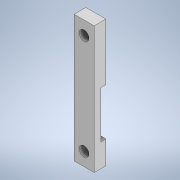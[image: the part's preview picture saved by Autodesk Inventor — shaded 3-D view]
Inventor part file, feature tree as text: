
AUTODESK INVENTOR PART (.ipt)
format: ipt  version: 2021 (Build 250183000, 183)  size: 128,000 bytes
history: native  units: in
note: dims shown in document units (in); Inventor stores cm internally (conversion verified against a paired STEP export)
features: other x3, extrude x2, sketch x2, reference x2, projected_geometry x2, plane x1
ambient origin geometry x8: Origin, YZ Plane, XZ Plane, XY Plane, X Axis, Y Axis, Z Axis, Center Point
bodies: Solid1 (feature_tree)
feature tree (12):
  plane  "Work Plane1"
  extrude  "Extrusion1"  Depth=0.0787in
  extrude  "Extrusion2"  Depth=0.0787in
  sketch  "Sketch1"  dims[d0=0.1575in d1=0.0787in]
  reference  "Reference1"
  reference  "Reference2"
  sketch  "Sketch2"  dims[d2=0.0394in d3=0.1575in d4=0.1181in d6=0.1181in d7=0.0591in d8=0.0in d9=0.0787in d10=0.0in]
  projected_geometry  "Projected Loop1"
  projected_geometry  "Projected Loop2"
  parser-record x1  (decoder bookkeeping rows leaked as tree rows — omitted from the tree; the rows remain in map.json)
  other  "assembly.iam"
  other  "gps_plate:1"
note: 1 file-system path scrubbed to <path> (originals preserved in map.json)
